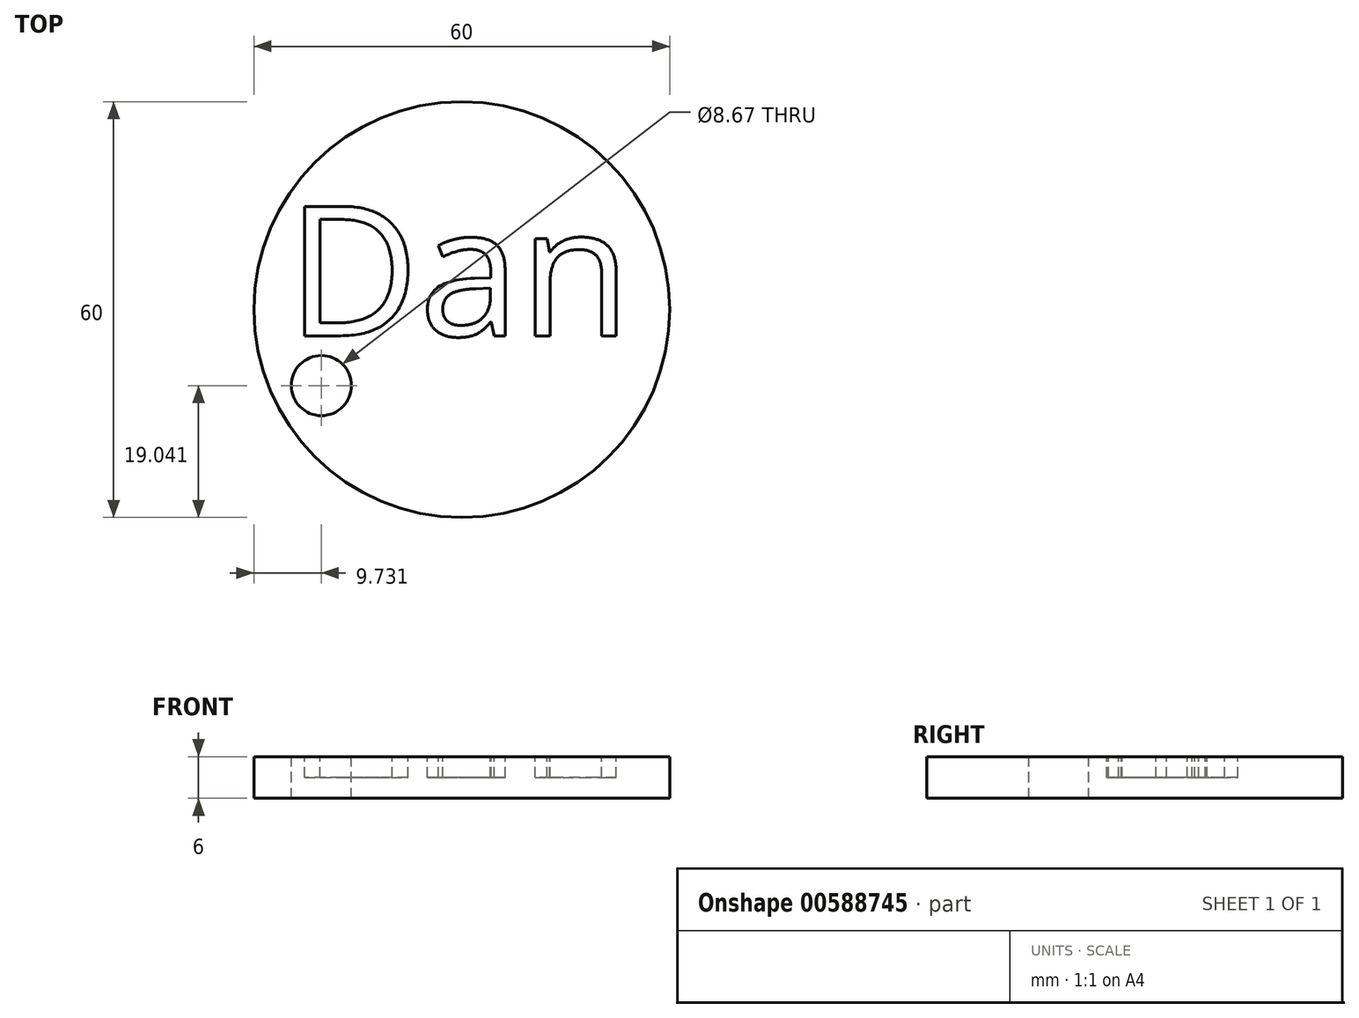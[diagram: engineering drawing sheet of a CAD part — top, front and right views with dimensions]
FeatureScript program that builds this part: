
annotation { "Feature Type Name" : "Feature", "Feature Type Description" : "" }
export const myFeature = defineFeature(function(context is Context, id is Id, definition is map)
    precondition{}
    {
        {
            var Q0;
            Q0=qCreatedBy(makeId("Top.planeOp"),FACE);
            var sketch = newSketch(context, id + "F0", { "sketchPlane" : qUnion([Q0])});
            skCircle(sketch, "E0", {"center": v(0, 0) * mm, "radius": 30 * mm});
            skSolve(sketch);
        }
        {
            var Q0;
            Q0=makeQuery(id+"F0.imprint","IMPRINT",FACE,{"disambiguationData":[TD([[makeQuery(id+"F0.imprint","IMPRINT",EDGE,{"derivedFrom":sQuery(id+"F0.wireOp",EDGE,"E0")}),1.0]])]});
            extrude(context, id + "F1", {"entities" : qUnion([Q0]), "depth" : 6 * mm, "offsetDistance" : 25 * mm, "symmetric" : true});
        }
        {
            var Q0;
            Q0=makeQuery(id+"F1.opExtrude","CAP_FACE",FACE,{"disambiguationData":[OSD([sQuery(id+"F0.wireOp",EDGE,"E0")])],"isStart":false});
            var sketch = newSketch(context, id + "F2", { "sketchPlane" : qUnion([Q0])});
            skCircle(sketch, "E1", {"center": v(-20.27, -10.96) * mm, "radius": 4.34 * mm});
            skSolve(sketch);
        }
        {
            var Q0;
            Q0=makeQuery(id+"F2.imprint","IMPRINT",FACE,{"disambiguationData":[TD([[makeQuery(id+"F2.imprint","IMPRINT",EDGE,{"derivedFrom":sQuery(id+"F2.wireOp",EDGE,"E1")}),1.0]])]});
            extrude(context, id + "F3", {"entities" : qUnion([Q0]), "operationType" : NewBodyOperationType.REMOVE, "oppositeDirection" : true, "depth" : 6 * mm, "offsetDistance" : 25 * mm});
        }
        {
            var Q0;
            Q0=makeQuery(id+"F1.opExtrude","CAP_FACE",FACE,{"disambiguationData":[OSD([sQuery(id+"F0.wireOp",EDGE,"E0")])],"isStart":false});
            var sketch = newSketch(context, id + "F4", { "sketchPlane" : qUnion([Q0])});
            skText(sketch, "E2", { "text": "Dan", "fontName": "OpenSans-Regular.ttf"});
            const initialGuessF4  = {"E2": [-0.02522, -0.00378, 1, 0, 0.01881]};
            skSetInitialGuess(sketch, initialGuessF4);
            skSolve(sketch);
        }
        {
            var Q0;
            Q0 = qSketchRegion(id + "F4", true);
            extrude(context, id + "F5", {"entities" : qUnion([Q0]), "operationType" : NewBodyOperationType.REMOVE, "oppositeDirection" : true, "depth" : 3 * mm, "offsetDistance" : 25 * mm});
        }
    });
